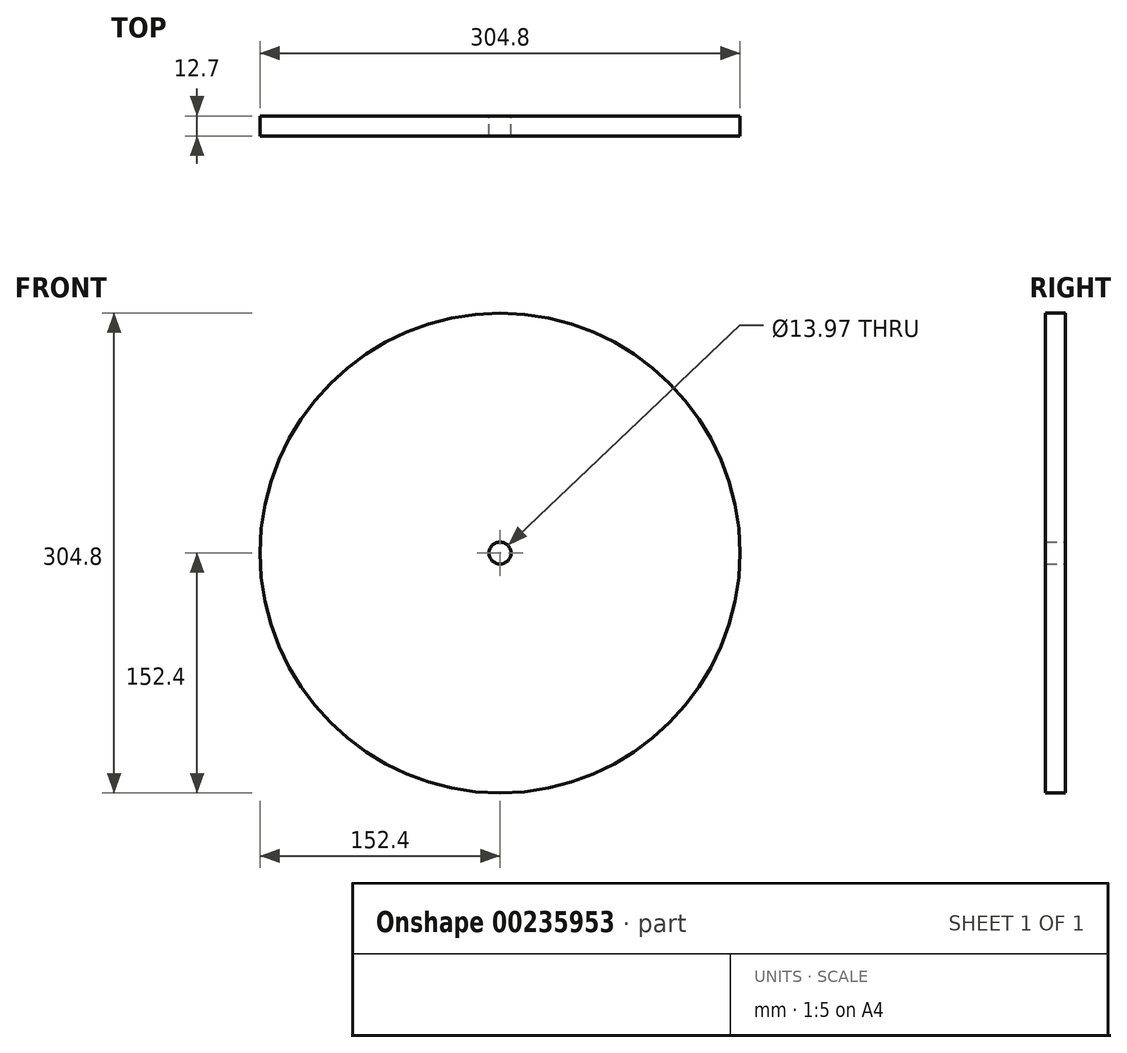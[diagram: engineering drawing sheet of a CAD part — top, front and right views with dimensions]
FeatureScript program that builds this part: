
annotation { "Feature Type Name" : "Feature", "Feature Type Description" : "" }
export const myFeature = defineFeature(function(context is Context, id is Id, definition is map)
    precondition{}
    {
        {
            var Q0;
            Q0=qCreatedBy(makeId("Front.planeOp"),FACE);
            var sketch = newSketch(context, id + "F0", { "sketchPlane" : qUnion([Q0])});
            skCircle(sketch, "E0", {"center": v(0, 0) * mm, "radius": 152.4 * mm});
            skCircle(sketch, "E1", {"center": v(0, 0) * mm, "radius": 6.99 * mm});
            skSolve(sketch);
        }
        {
            var Q0;
            Q0=makeQuery(id+"F0.imprint","IMPRINT",FACE,{"disambiguationData":[TD([[makeQuery(id+"F0.imprint","IMPRINT",EDGE,{"derivedFrom":sQuery(id+"F0.wireOp",EDGE,"E0")}),1.0]])]});
            extrude(context, id + "F1", {"entities" : qUnion([Q0]), "depth" : 12.7 * mm});
        }
    });
